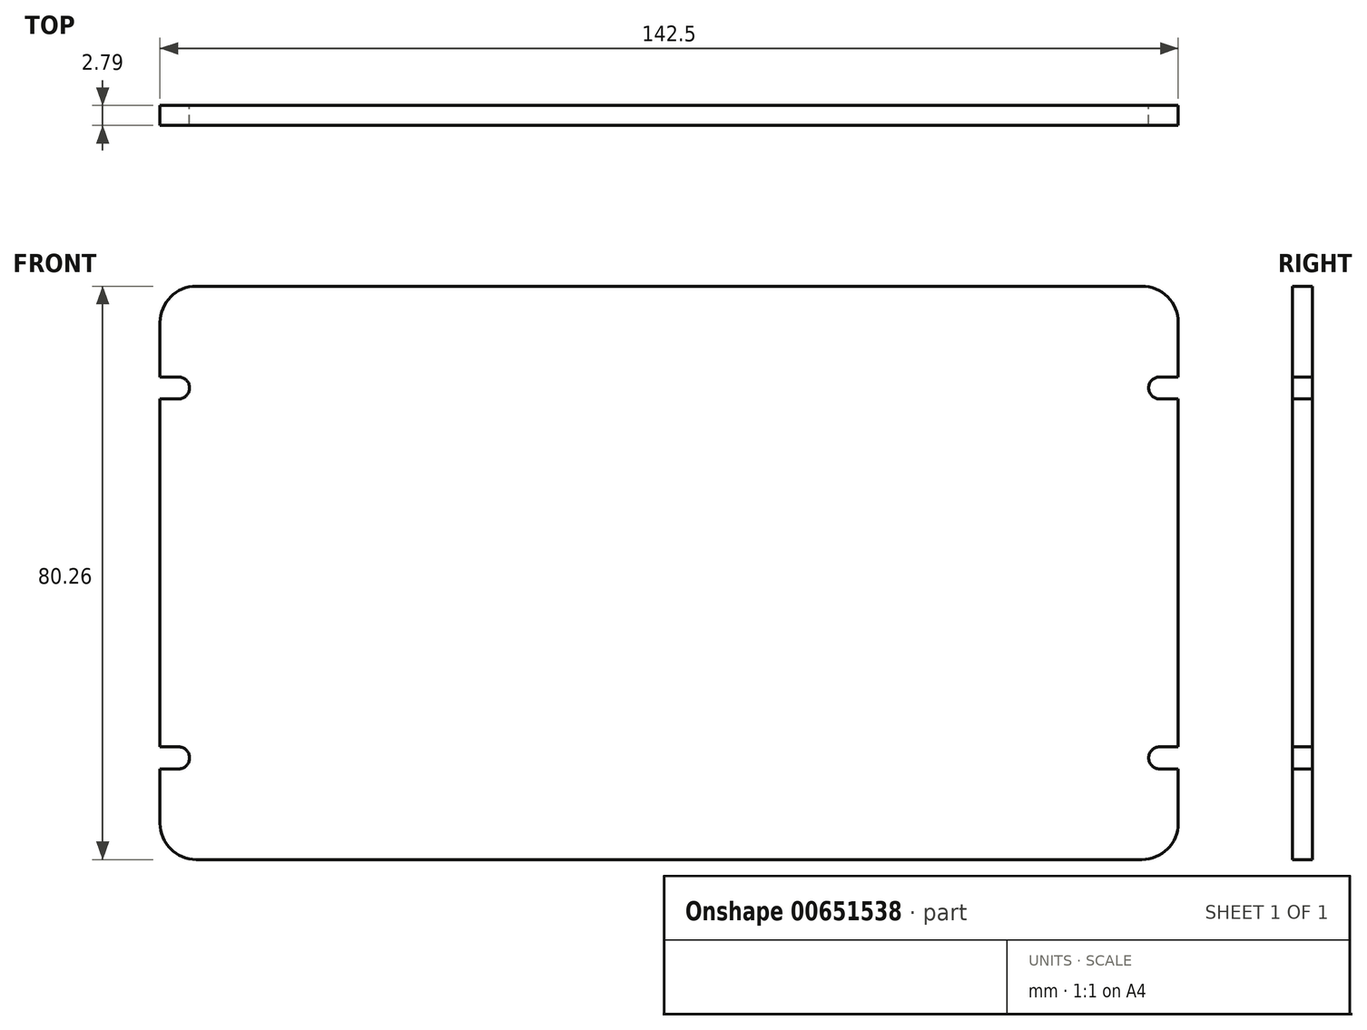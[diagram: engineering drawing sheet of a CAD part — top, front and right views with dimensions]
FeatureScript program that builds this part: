
annotation { "Feature Type Name" : "Feature", "Feature Type Description" : "" }
export const myFeature = defineFeature(function(context is Context, id is Id, definition is map)
    precondition{}
    {
        {
            var Q0;
            Q0=qCreatedBy(makeId("Front.planeOp"),FACE);
            var sketch = newSketch(context, id + "F0", { "sketchPlane" : qUnion([Q0])});
            skLineSegment(sketch, "E0.bottom", {"start": v(66.17, 40.13) * mm, "end": v(-66.17, 40.13) * mm});
            skLineSegment(sketch, "E0.top", {"start": v(66.17, -40.13) * mm, "end": v(-66.17, -40.13) * mm});
            skLineSegment(sketch, "E0.left", {"start": v(71.25, 35.05) * mm, "end": v(71.25, 27.43) * mm});
            skLineSegment(sketch, "E0.right", {"start": v(-71.25, 35.05) * mm, "end": v(-71.25, 27.43) * mm});
            skPoint(sketch, "E0.middle", {"position": v(0, 0) * mm});
            skPoint(sketch, "E1.visualSharp", {"position": v(-71.25, 40.13) * mm});
            skArc(sketch, "E1.filletArc", {"start": v(-66.17, 40.13) * mm, "mid": v(-69.76, 38.64) * mm, "end": v(-71.25, 35.05) * mm});
            skPoint(sketch, "E2.visualSharp", {"position": v(71.25, 40.13) * mm});
            skArc(sketch, "E2.filletArc", {"start": v(71.25, 35.05) * mm, "mid": v(69.76, 38.64) * mm, "end": v(66.17, 40.13) * mm});
            skPoint(sketch, "E3.visualSharp", {"position": v(71.25, -40.13) * mm});
            skArc(sketch, "E3.filletArc", {"start": v(66.17, -40.13) * mm, "mid": v(69.76, -38.64) * mm, "end": v(71.25, -35.05) * mm});
            skPoint(sketch, "E4.visualSharp", {"position": v(-71.25, -40.13) * mm});
            skArc(sketch, "E4.filletArc", {"start": v(-71.25, -35.05) * mm, "mid": v(-69.76, -38.64) * mm, "end": v(-66.17, -40.13) * mm});
            skLineSegment(sketch, "E5.bottom", {"start": v(-71.25, 27.43) * mm, "end": v(-68.64, 27.43) * mm});
            skLineSegment(sketch, "E5.top", {"start": v(-71.25, 24.36) * mm, "end": v(-68.64, 24.36) * mm});
            skArc(sketch, "E6", {"start": v(-68.64, 27.43) * mm, "mid": v(-67.1, 25.9) * mm, "end": v(-68.64, 24.36) * mm});
            skLineSegment(sketch, "E7.trimOffspring", {"start": v(-71.25, 24.36) * mm, "end": v(-71.25, -24.36) * mm});
            skLineSegment(sketch, "E8.MirrorCS", {"start": v(71.25, 27.43) * mm, "end": v(68.64, 27.43) * mm});
            skLineSegment(sketch, "E9.MirrorCS", {"start": v(71.25, 24.36) * mm, "end": v(68.64, 24.36) * mm});
            skArc(sketch, "E10.MirrorCS", {"start": v(68.64, 27.43) * mm, "mid": v(67.1, 25.9) * mm, "end": v(68.64, 24.36) * mm});
            skLineSegment(sketch, "E11.trimOffspring", {"start": v(71.25, 24.36) * mm, "end": v(71.25, -24.36) * mm});
            skLineSegment(sketch, "E12.MirrorCS", {"start": v(71.25, -27.43) * mm, "end": v(68.64, -27.43) * mm});
            skLineSegment(sketch, "E13.MirrorCS", {"start": v(71.25, -24.36) * mm, "end": v(68.64, -24.36) * mm});
            skArc(sketch, "E14.MirrorCS", {"start": v(68.64, -27.43) * mm, "mid": v(67.1, -25.9) * mm, "end": v(68.64, -24.36) * mm});
            skLineSegment(sketch, "E15.MirrorCS", {"start": v(71.25, -24.36) * mm, "end": v(71.25, 24.36) * mm});
            skLineSegment(sketch, "E16.MirrorCS", {"start": v(-71.25, -27.43) * mm, "end": v(-68.64, -27.43) * mm});
            skArc(sketch, "E17.MirrorCS", {"start": v(-68.64, -27.43) * mm, "mid": v(-67.1, -25.9) * mm, "end": v(-68.64, -24.36) * mm});
            skLineSegment(sketch, "E18.MirrorCS", {"start": v(-71.25, -24.36) * mm, "end": v(-68.64, -24.36) * mm});
            skLineSegment(sketch, "E19.trimOffspring", {"start": v(-71.25, -27.43) * mm, "end": v(-71.25, -35.05) * mm});
            skLineSegment(sketch, "E20.trimOffspring", {"start": v(71.25, -27.43) * mm, "end": v(71.25, -35.05) * mm});
            skLineSegment(sketch, "E21.trimOffspring", {"start": v(71.25, 27.43) * mm, "end": v(71.25, 35.05) * mm});
            skSolve(sketch);
        }
        {
            var Q0;
            Q0 = qSketchRegion(id + "F0", true);
            extrude(context, id + "F1", {"entities" : qUnion([Q0]), "depth" : 2.8 * mm, "offsetDistance" : 25.4 * mm});
        }
    });
